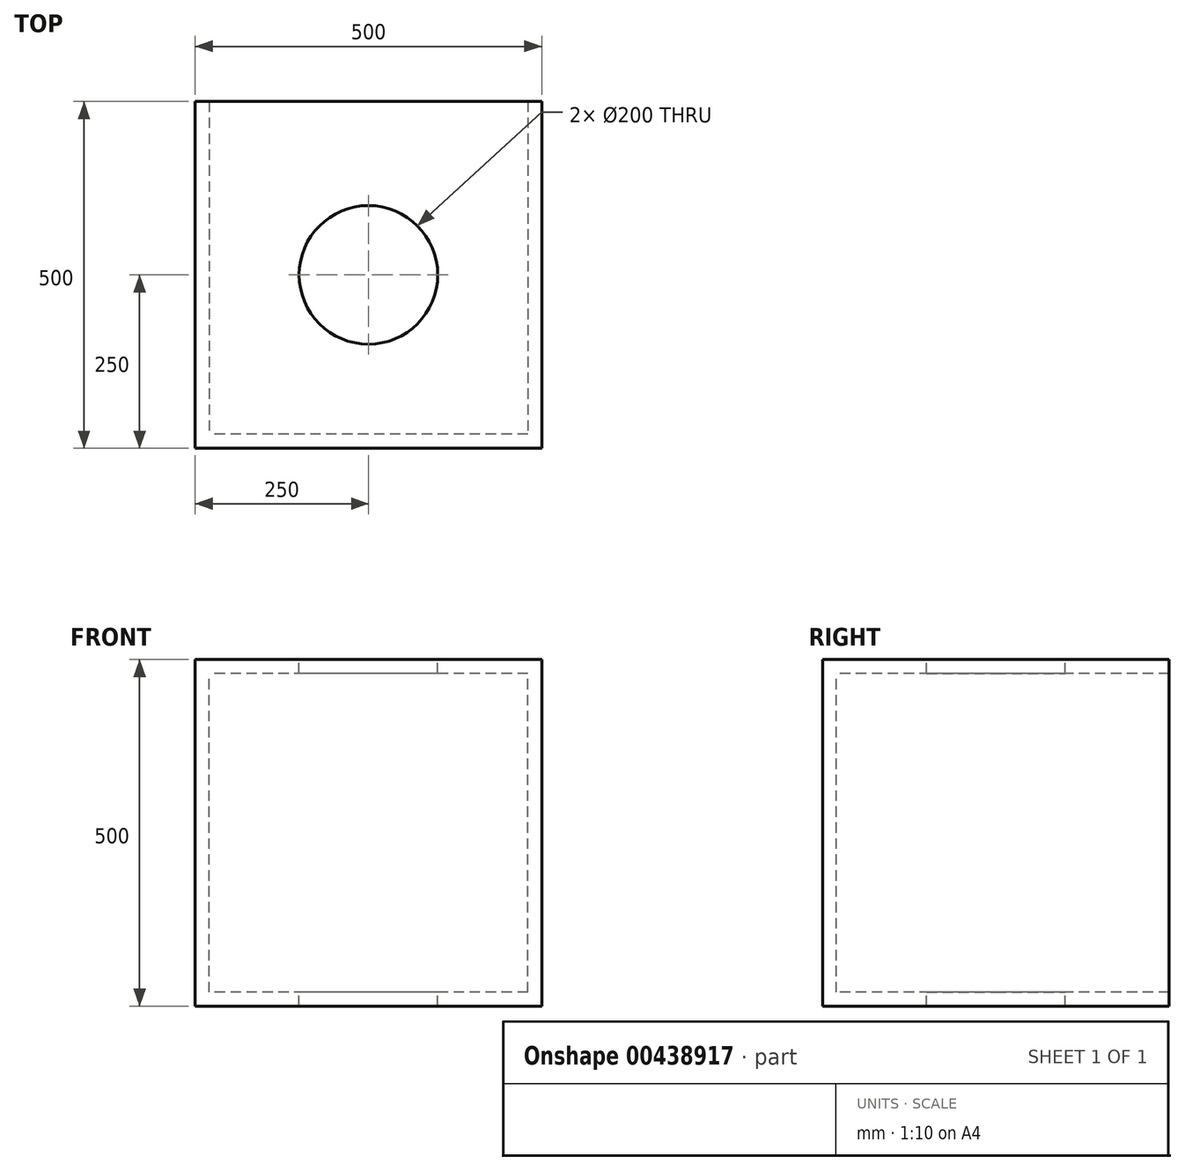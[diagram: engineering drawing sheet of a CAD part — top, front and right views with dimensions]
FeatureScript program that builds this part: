
annotation { "Feature Type Name" : "Feature", "Feature Type Description" : "" }
export const myFeature = defineFeature(function(context is Context, id is Id, definition is map)
    precondition{}
    {
        {
            var Q0;
            Q0=qCreatedBy(makeId("Front.planeOp"),FACE);
            var sketch = newSketch(context, id + "F0", { "sketchPlane" : qUnion([Q0])});
            skLineSegment(sketch, "E0.bottom", {"start": v(250, -250) * mm, "end": v(-250, -250) * mm});
            skLineSegment(sketch, "E0.top", {"start": v(250, 250) * mm, "end": v(-250, 250) * mm});
            skLineSegment(sketch, "E0.left", {"start": v(250, -250) * mm, "end": v(250, 250) * mm});
            skLineSegment(sketch, "E0.right", {"start": v(-250, -250) * mm, "end": v(-250, 250) * mm});
            skPoint(sketch, "E0.middle", {"position": v(0, 0) * mm});
            skSolve(sketch);
        }
        {
            var Q0;
            Q0=makeQuery(id+"F0.imprint","IMPRINT",FACE,{"disambiguationData":[TD([[makeQuery(id+"F0.imprint","IMPRINT",EDGE,{"derivedFrom":sQuery(id+"F0.wireOp",EDGE,"E0.bottom")}),-1.0]])]});
            extrude(context, id + "F1", {"entities" : qUnion([Q0]), "oppositeDirection" : true, "depth" : 500 * mm});
        }
        {
            var Q0;
            Q0=makeQuery(id+"F1.opExtrude","CAP_FACE",FACE,{"disambiguationData":[OSD([sQuery(id+"F0.wireOp",EDGE,"E0.bottom"),sQuery(id+"F0.wireOp",EDGE,"E0.top"),sQuery(id+"F0.wireOp",EDGE,"E0.left"),sQuery(id+"F0.wireOp",EDGE,"E0.right")])],"isStart":false});
            shell(context, id + "F2", {"entities" : qUnion([Q0]), "thickness" : 20 * mm});
        }
        {
            var Q0;
            Q0=makeQuery(id+"F1.opExtrude","SWEPT_FACE",FACE,{"disambiguationData":[OSD([sQuery(id+"F0.wireOp",EDGE,"E0.top")])]});
            var sketch = newSketch(context, id + "F3", { "sketchPlane" : qUnion([Q0])});
            skCircle(sketch, "E1", {"center": v(0, 250) * mm, "radius": 100 * mm});
            skSolve(sketch);
        }
        {
            var Q0;
            Q0 = qSketchRegion(id + "F3", true);
            extrude(context, id + "F4", {"entities" : qUnion([Q0]), "operationType" : NewBodyOperationType.ADD, "depth" : 25 * mm});
        }
        {
            var Q0;
            Q0=makeQuery(id+"F4.opExtrude","CAP_FACE",FACE,{"disambiguationData":[OSD([sQuery(id+"F3.wireOp",EDGE,"E1")])],"isStart":false});
            extrude(context, id + "F5", {"entities" : qUnion([Q0]), "operationType" : NewBodyOperationType.REMOVE, "endBound" : BoundingType.THROUGH_ALL, "oppositeDirection" : true, "depth" : 25 * mm});
        }
    });
